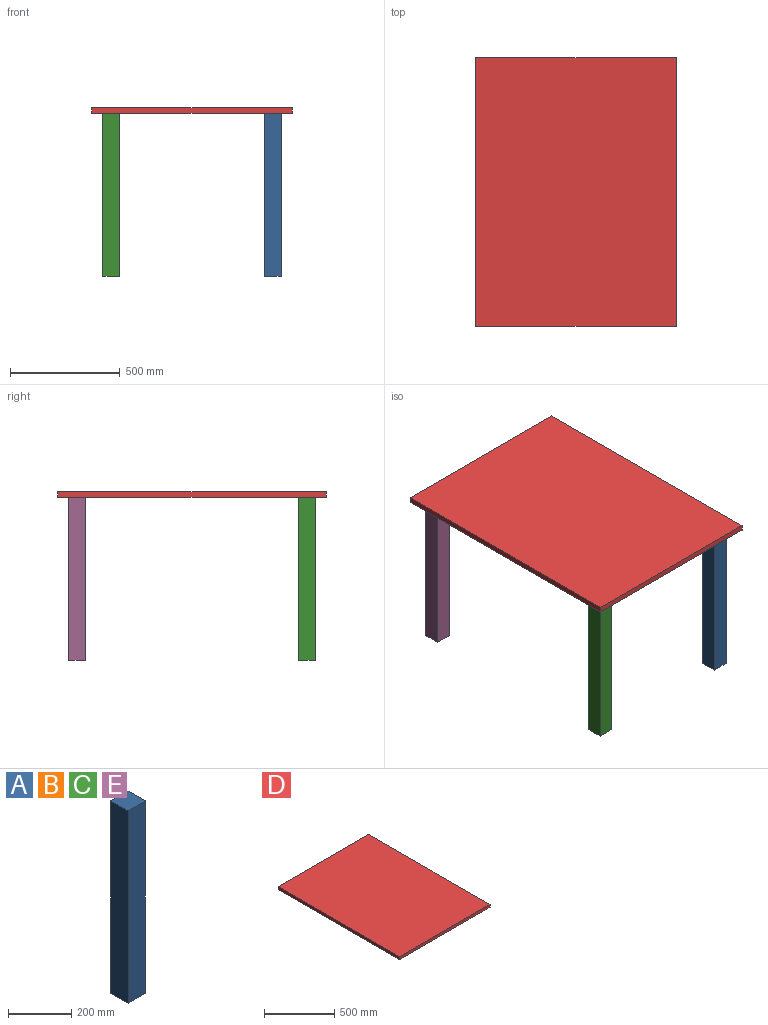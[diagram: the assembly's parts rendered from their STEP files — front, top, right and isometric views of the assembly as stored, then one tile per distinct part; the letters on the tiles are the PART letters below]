
ASSEMBLY  parts=5 mates=4
PART A: 6 faces, bbox 76.2x76.2x743 mm
  f0: plane 742.95x76.2mm, normal (0,1,0), area 56612.8mm2, adj f1,f3,f4,f5
  f1: plane 742.95x76.2mm, normal (1,0,0), area 56612.8mm2, adj f0,f2,f4,f5
  f2: plane 742.95x76.2mm, normal (0,-1,0), area 56612.8mm2, adj f1,f3,f4,f5
  f3: plane 742.95x76.2mm, normal (-1,0,0), area 56612.8mm2, adj f0,f2,f4,f5
  f4: plane 76.2x76.2mm, normal (0,0,-1), area 5806.4mm2, adj f0,f1,f2,f3
  f5: plane 76.2x76.2mm, normal (0,0,1), area 5806.4mm2, adj f0,f1,f2,f3
PART B: same geometry as A
PART C: same geometry as A
PART D: 6 faces, bbox 914.4x1225.6x25.4 mm
  f0: plane 914.4x25.4mm, normal (0,1,0), area 23225.8mm2, adj f1,f3,f4,f5
  f1: plane 1225.55x25.4mm, normal (-1,0,0), area 31129mm2, adj f0,f2,f4,f5
  f2: plane 914.4x25.4mm, normal (0,-1,0), area 23225.8mm2, adj f1,f3,f4,f5
  f3: plane 1225.55x25.4mm, normal (1,0,0), area 31129mm2, adj f0,f2,f4,f5
  f4: plane 1225.55x914.4mm, normal (0,0,-1), area 1120642.9mm2, adj f0,f1,f2,f3
  f5: plane 1225.55x914.4mm, normal (0,0,1), area 1120642.9mm2, adj f0,f1,f2,f3
PART E: same geometry as A
PLACE A at identity
PLACE B t=(0,1047.75,0)mm
PLACE C t=(-736.6,0,0)mm
PLACE D at identity fixed
PLACE E t=(-736.6,1047.75,0)mm
MATE fastened A.f5 <-> D.f4  axis (0,0,1) through (4671.32,-1720.18,768.35)mm
MATE fastened B.f5 <-> D.f4  axis (0,0,1) through (4671.32,-596.23,768.35)mm
MATE fastened E.f5 <-> D.f4  axis (0,0,1) through (3858.52,-596.23,768.35)mm
MATE fastened C.f5 <-> D.f4  axis (0,0,1) through (3858.52,-1720.18,768.35)mm
